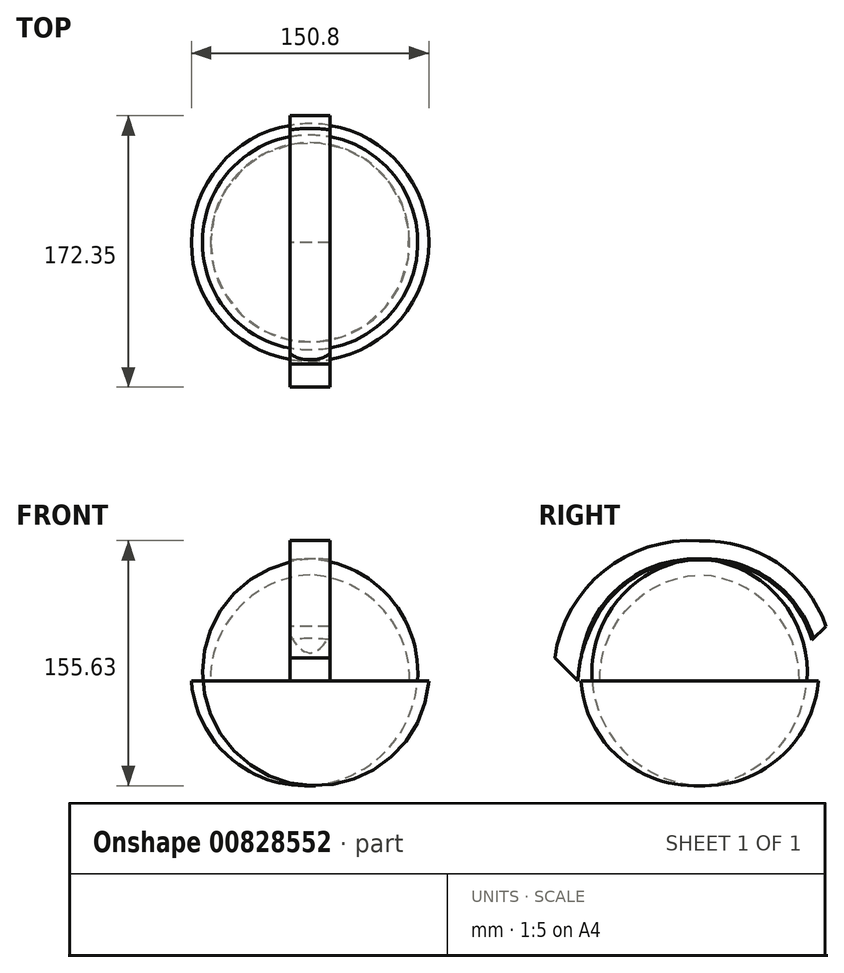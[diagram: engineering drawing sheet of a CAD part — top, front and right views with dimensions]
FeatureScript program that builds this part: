
annotation { "Feature Type Name" : "Feature", "Feature Type Description" : "" }
export const myFeature = defineFeature(function(context is Context, id is Id, definition is map)
    precondition{}
    {
        {
            var Q0;
            Q0=qCreatedBy(makeId("Front.planeOp"),FACE);
            var sketch = newSketch(context, id + "F0", { "sketchPlane" : qUnion([Q0])});
            skArc(sketch, "E0", {"start": v(0, 77.54) * mm, "mid": v(-55.23, 55.82) * mm, "end": v(-75.4, 0) * mm});
            skLineSegment(sketch, "E1", {"start": v(-75.4, 0) * mm, "end": v(-63.3, 0) * mm});
            skLineSegment(sketch, "E2", {"start": v(-63.3, 0) * mm, "end": v(-63.3, 0) * mm});
            skLineSegment(sketch, "E3", {"start": v(0, 77.54) * mm, "end": v(0, 67.56) * mm});
            skArc(sketch, "E4", {"start": v(0, 67.56) * mm, "mid": v(-45.34, 46.6) * mm, "end": v(-63.3, 0) * mm});
            skSolve(sketch);
        }
        {
            var Q0;
            Q0 = qSketchRegion(id + "F0", true);
            var Q1;
            Q1=sQuery(id+"F0.wireOp",EDGE,"E3");
            revolve(context, id + "F1", {"surfaceOperationType" : NewSurfaceOperationType.NEW, "entities" : qUnion([Q0]), "axis" : qUnion([Q1]), "revolveType" : RevolveType.FULL});
        }
        {
            var Q0;
            Q0=qCreatedBy(makeId("Right.planeOp"),FACE);
            var sketch = newSketch(context, id + "F2", { "sketchPlane" : qUnion([Q0])});
            skArc(sketch, "E5", {"start": v(0, 88.98) * mm, "mid": v(-60.69, 70.06) * mm, "end": v(-91.96, 14.72) * mm});
            skArc(sketch, "E6", {"start": v(80.4, 34.74) * mm, "mid": v(49.22, 75.23) * mm, "end": v(0, 88.98) * mm});
            skLineSegment(sketch, "E7", {"start": v(80.4, 34.74) * mm, "end": v(68.82, 23.68) * mm});
            skArc(sketch, "E8", {"start": v(68.82, 23.68) * mm, "mid": v(-14.01, 72.5) * mm, "end": v(-77.16, 0) * mm});
            skLineSegment(sketch, "E9", {"start": v(-77.16, 0) * mm, "end": v(-91.96, 14.72) * mm});
            skSolve(sketch);
        }
        {
            var Q0;
            Q0 = qSketchRegion(id + "F2", true);
            extrude(context, id + "F3", {"entities" : qUnion([Q0]), "operationType" : NewBodyOperationType.ADD, "endBound" : BoundingType.SYMMETRIC, "depth" : 25.4 * mm, "offsetDistance" : 25.4 * mm});
        }
    });
